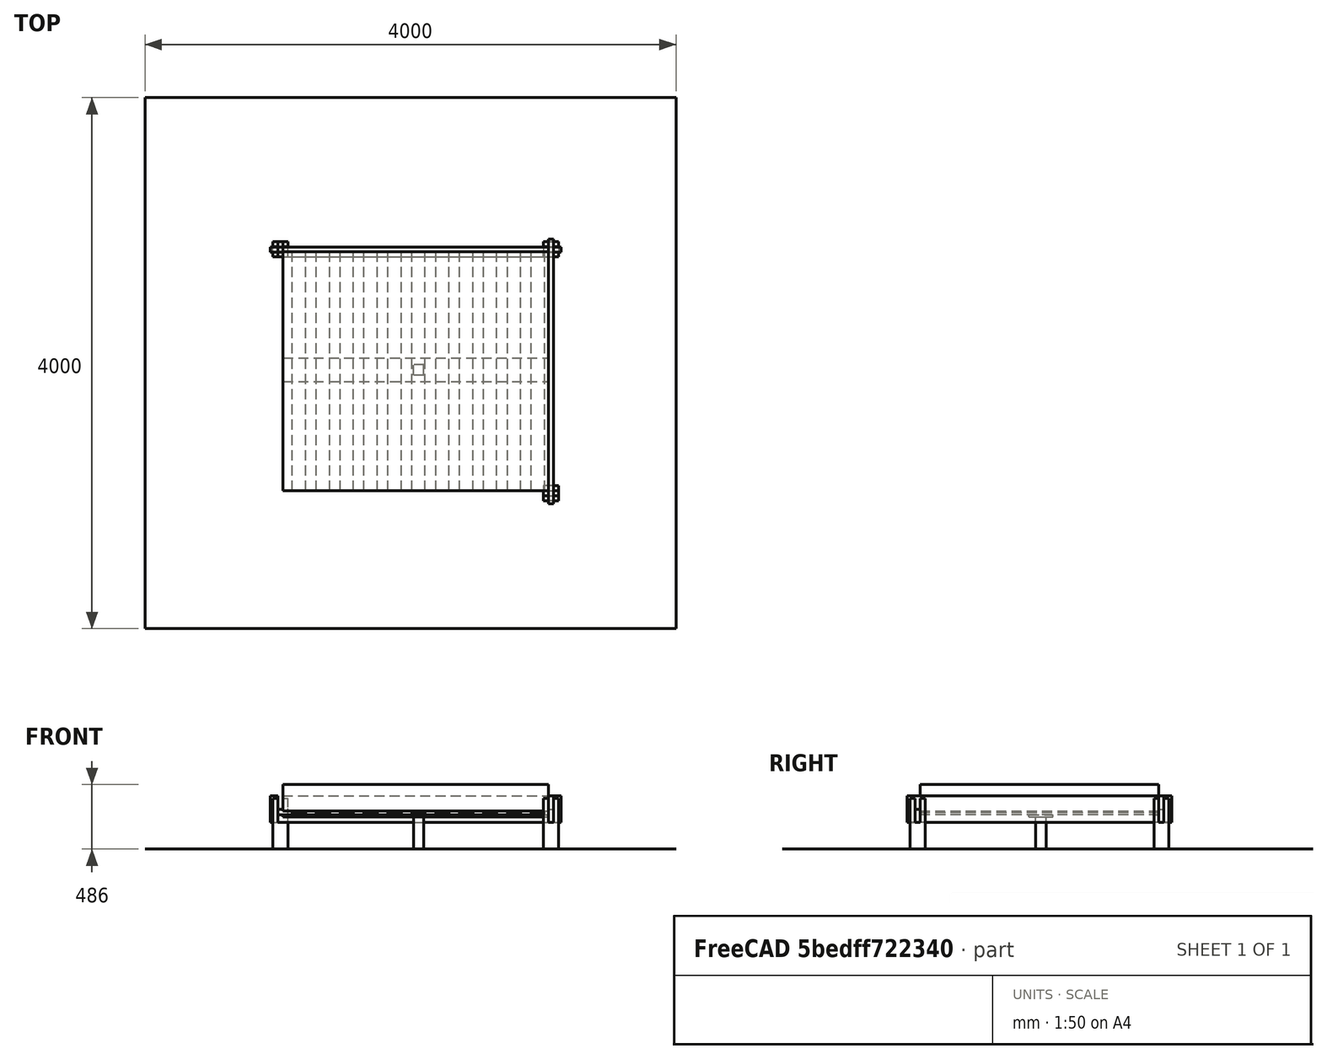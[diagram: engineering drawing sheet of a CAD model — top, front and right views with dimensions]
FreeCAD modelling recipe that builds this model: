
FCSTD DOCUMENT  (FreeCAD 0.18RUnknown)
Label: bett
License: All rights reserved
LicenseURL: http://en.wikipedia.org/wiki/All_rights_reserved
objects: Part::Box×18, TechDraw::DrawViewDimension×15, Part::FeaturePython×7, Part::Cut×4, TechDraw::DrawProjGroup×3, TechDraw::DrawProjGroupItem×2, App::DocumentObjectGroup×2, TechDraw::DrawViewPart×2, Part::MultiFuse×1, TechDraw::DrawSVGTemplate×1, TechDraw::DrawPage×1
note: 30 computed .brp shape members not serialized (recipe doc carries the construction recipe); baked Part::Feature solids carry a one-line shape summary decoded from their .brp

FEATURE [Part::Box] Box  label="Cube"
  AttacherType = Attacher::AttachEngine3D
  Height = 200
  Length = 76
  Width = 76
FEATURE [Part::Box] Box001  label="lang-1"
  AttacherType = Attacher::AttachEngine3D
  Height = 380
  Length = 38
  Placement = pos=(-38,0,0) rot=(0,0,1;0rad)
  Width = 38
FEATURE [Part::Box] Box002  label="lang-2"
  AttacherType = Attacher::AttachEngine3D
  Height = 380
  Length = 38
  Placement = pos=(38,76,0) rot=(0,0,1;0rad)
  Width = 38
FEATURE [Part::Box] Box003  label="lang-3"
  AttacherType = Attacher::AttachEngine3D
  Height = 380
  Length = 38
  Placement = pos=(-38,76,0) rot=(0,0,1;0rad)
  Width = 38
FEATURE [Part::Box] Box004  label="Cube004"
  AttacherType = Attacher::AttachEngine3D
  Height = 200
  Length = 38
  Placement = pos=(-38,38,0) rot=(0,0,1;0rad)
  Width = 38
FEATURE [Part::Box] Box005  label="Cube005"
  AttacherType = Attacher::AttachEngine3D
  Height = 200
  Length = 38
  Placement = pos=(0,76,0) rot=(0,0,1;0rad)
  Width = 38
FEATURE [Part::MultiFuse] Fusion  label="VR"
  Placement = pos=(76,0,0) rot=(0,0,1;1.5708rad)
  Shapes = -> [Box,Box001,Box002,Box003,Box004,Box005]
FEATURE [Part::Box] Box015  label="R"
  AttacherType = Attacher::AttachEngine3D
  Height = 200
  Length = 2192
  Placement = pos=(-58,0,200) rot=(0,0,1;0rad)
  Width = 38
FEATURE [Part::Box] Box017  label="V"
  AttacherType = Attacher::AttachEngine3D
  Height = 200
  Length = 1992
  Placement = pos=(38,-58,200) rot=(0,0,1;1.5708rad)
  Width = 38
FEATURE [Part::Box] Box019  label="Matratze"
  AttacherType = Attacher::AttachEngine3D
  Height = 200
  Length = 2000
  Placement = pos=(38,38,285) rot=(0,0,1;0rad)
  Width = 1800
FEATURE [Part::Box] Box020  label="Querstrebe"
  AttacherType = Attacher::AttachEngine3D
  Height = 18
  Length = 2000
  Placement = pos=(40,860,240) rot=(0,0,1;0rad)
  Width = 180
FEATURE [Part::Box] Box021  label="Mittelpfosten"
  AttacherType = Attacher::AttachEngine3D
  Height = 78
  Length = 240
  Placement = pos=(1100,910,1.63e-13) rot=(0,-1,0;1.5708rad)
  Width = 78
FEATURE [Part::Box] Box022  label="Rost"
  AttacherType = Attacher::AttachEngine3D
  Height = 18
  Length = 1800
  Placement = pos=(110,0,277) rot=(0.707107,0.707107,0;3.14159rad)
  Width = 100
FEATURE [Part::Box] Box023  label="V001"
  AttacherType = Attacher::AttachEngine3D
  Height = 100
  Length = 200
  Placement = pos=(-100,0,200) rot=(0,0,1;0rad)
  Width = 38
FEATURE [Part::Cut] Cut
  Base = -> Box017
  Tool = -> Box023
FEATURE [Part::Box] Box024  label="H001"
  AttacherType = Attacher::AttachEngine3D
  Height = 100
  Length = 200
  Placement = pos=(-100,1838,200) rot=(0,0,1;0rad)
  Width = 38
FEATURE [Part::Cut] Cut001  label="S-V"
  Base = -> Cut
  Tool = -> Box024
FEATURE [Part::Box] Box026  label="L002"
  AttacherType = Attacher::AttachEngine3D
  Height = 100
  Length = 200
  Placement = pos=(38,-100,300) rot=(0,0,1;1.5708rad)
  Width = 38
FEATURE [Part::Cut] Cut003
  Base = -> Box015
  Tool = -> Box026
FEATURE [Part::Box] Box027  label="L003"
  AttacherType = Attacher::AttachEngine3D
  Height = 100
  Length = 200
  Placement = pos=(2076,-100,300) rot=(0,0,1;1.5708rad)
  Width = 38
FEATURE [Part::Cut] Cut004  label="S-R"
  Base = -> Cut003
  Tool = -> Box027
FEATURE [Part::FeaturePython] Array  # Draft array (typed FeaturePython)
  Angle = 360
  ArrayType = 0
  Axis = (0,0,1)
  Base = -> Box022
  Center = (0,0,0)
  Fuse = false
  IntervalAxis = (0,0,0)
  IntervalX = (180,0,0)
  IntervalY = (0,1,0)
  IntervalZ = (0,0,1)
  NumberPolar = 1
  NumberX = 11
  NumberY = 2
  NumberZ = 1
  Placement = pos=(0,38,0) rot=(0,0,1;0rad)
FEATURE [Part::Box] Box031  label="Rostauflage R"
  AttacherType = Attacher::AttachEngine3D
  Height = 58
  Length = 2000
  Placement = pos=(0,38,200) rot=(0,0,1;0rad)
  Width = 38
FEATURE [Part::Box] Box033  label="Boden"
  AttacherType = Attacher::AttachEngine3D
  Height = 1
  Length = 4000
  Placement = pos=(-1000,-1000,-1) rot=(0,0,1;0rad)
  Width = 4000
FEATURE [TechDraw::DrawSVGTemplate] Template
  Height = 210
  Orientation = 1
  Width = 297
FEATURE [TechDraw::DrawProjGroupItem] ProjItem  label="Kurze Seiten"
  CoarseView = false
  Direction = (1,0,0)
  Focus = 100
  HardHidden = false
  IsoCount = 0
  IsoHidden = false
  IsoVisible = false
  LockPosition = true
  Perspective = false
  Rotation = 0
  RotationVector = (0,1,0)
  Scale = 0.1
  ScaleType = 2
  SeamHidden = false
  SeamVisible = false
  SmoothHidden = false
  SmoothVisible = false
  Type = 0
  X = 0
  Y = 0
FEATURE [TechDraw::DrawProjGroup] ProjGroup
  Anchor = -> ProjItem
  AutoDistribute = true
  LockPosition = false
  ProjectionType = 0
  Rotation = 0
  Scale = 0.1
  ScaleType = 0
  Views = -> [ProjItem]
  X = 154.536
  Y = 169.749
  spacingX = 15
  spacingY = 15
FEATURE [TechDraw::DrawViewDimension] Dimension
  Arbitrary = false
  FormatSpec = %.2f
  LockPosition = false
  MeasureType = 1
  OverTolerance = 0
  References2D = -> [ProjItem]
  Rotation = 0
  ScaleType = 0
  Type = 0
  UnderTolerance = 0
  X = 1.3039
  Y = 17.0645
FEATURE [TechDraw::DrawViewDimension] Dimension001
  Arbitrary = false
  FormatSpec = %.2f
  LockPosition = false
  MeasureType = 1
  OverTolerance = 0
  References2D = -> [ProjItem]
  Rotation = 0
  ScaleType = 0
  Type = 2
  UnderTolerance = 0
  X = -85.072
  Y = 0.024594
FEATURE [TechDraw::DrawViewDimension] Dimension002
  Arbitrary = false
  FormatSpec = %.2f
  LockPosition = false
  MeasureType = 1
  OverTolerance = 0
  References2D = -> [ProjItem]
  Rotation = 0
  ScaleType = 0
  Type = 1
  UnderTolerance = 0
  X = -110.228
  Y = -12.9954
FEATURE [TechDraw::DrawViewDimension] Dimension003
  Arbitrary = false
  FormatSpec = %.2f
  LockPosition = false
  MeasureType = 1
  OverTolerance = 0
  References2D = -> [ProjItem]
  Rotation = 0
  ScaleType = 0
  Type = 1
  UnderTolerance = 0
  X = -79.3385
  Y = -19.6627
FEATURE [TechDraw::DrawViewDimension] Dimension004
  Arbitrary = false
  FormatSpec = %.2f
  LockPosition = false
  MeasureType = 1
  OverTolerance = 0
  References2D = -> [ProjItem]
  Rotation = 0
  ScaleType = 0
  Type = 2
  UnderTolerance = 0
  X = -107.983
  Y = 0.457269
FEATURE [TechDraw::DrawProjGroupItem] ProjItem001  label="Lange Seiten"
  CoarseView = false
  Direction = (0,-1,0)
  Focus = 100
  HardHidden = false
  IsoCount = 0
  IsoHidden = false
  IsoVisible = false
  LockPosition = true
  Perspective = false
  Rotation = 0
  RotationVector = (1,0,0)
  Scale = 0.1
  ScaleType = 2
  SeamHidden = false
  SeamVisible = false
  SmoothHidden = false
  SmoothVisible = false
  Source = -> [Cut004]
  Type = 0
  X = 0
  Y = 0
FEATURE [TechDraw::DrawProjGroup] ProjGroup001
  Anchor = -> ProjItem001
  AutoDistribute = true
  LockPosition = false
  ProjectionType = 0
  Rotation = 0
  Scale = 0.1
  ScaleType = 0
  Source = -> [Cut004]
  Views = -> [ProjItem001]
  X = 156.289
  Y = 114.626
  spacingX = 15
  spacingY = 15
FEATURE [TechDraw::DrawViewDimension] Dimension005
  Arbitrary = false
  FormatSpec = %.2f
  LockPosition = false
  MeasureType = 1
  OverTolerance = 0
  References2D = -> [ProjItem001]
  Rotation = 0
  ScaleType = 0
  Type = 1
  UnderTolerance = 0
  X = -120.062
  Y = 24.2428
FEATURE [TechDraw::DrawViewDimension] Dimension006
  Arbitrary = false
  FormatSpec = %.2f
  LockPosition = false
  MeasureType = 1
  OverTolerance = 0
  References2D = -> [ProjItem001]
  Rotation = 0
  ScaleType = 0
  Type = 1
  UnderTolerance = 0
  X = -88.9728
  Y = 19.6663
FEATURE [TechDraw::DrawViewDimension] Dimension007
  Arbitrary = false
  FormatSpec = %.2f
  LockPosition = false
  MeasureType = 1
  OverTolerance = 0
  References2D = -> [ProjItem001]
  Rotation = 0
  ScaleType = 0
  Type = 2
  UnderTolerance = 0
  X = -95.9239
  Y = -0.007839
FEATURE [TechDraw::DrawViewDimension] Dimension008
  Arbitrary = false
  FormatSpec = %.2f
  LockPosition = false
  MeasureType = 1
  OverTolerance = 0
  References2D = -> [ProjItem001]
  Rotation = 0
  ScaleType = 0
  Type = 1
  UnderTolerance = 0
  X = -1.80037
  Y = -13.564
FEATURE [TechDraw::DrawProjGroup] ProjGroup002
  AutoDistribute = true
  LockPosition = false
  ProjectionType = 0
  Rotation = 0
  Scale = 0.1
  ScaleType = 0
  X = 51.6303
  Y = 56.7766
  spacingX = 15
  spacingY = 15
FEATURE [TechDraw::DrawViewDimension] Dimension009
  Arbitrary = false
  FormatSpec = %.2f
  LockPosition = false
  MeasureType = 1
  OverTolerance = 0
  References2D = -> [ProjItem001]
  Rotation = 0
  ScaleType = 0
  Type = 2
  UnderTolerance = 0
  X = -117.994
  Y = -0.079621
FEATURE [Part::FeaturePython] Clone  label="VL"  # Draft clone (typed FeaturePython)
  AttacherType = Attacher::AttachEngine3D
  Fuse = false
  Objects = -> [Fusion]
  Placement = pos=(0,1800,0) rot=(0,0,1;0rad)
  Scale = (1,1,1)
FEATURE [Part::FeaturePython] Clone001  label="HL"  # Draft clone (typed FeaturePython)
  AttacherType = Attacher::AttachEngine3D
  Fuse = false
  Objects = -> [Fusion]
  Placement = pos=(2000,1876,0) rot=(0,0,1;4.71239rad)
  Scale = (1,1,1)
FEATURE [Part::FeaturePython] Clone002  label="HR"  # Draft clone (typed FeaturePython)
  AttacherType = Attacher::AttachEngine3D
  Fuse = false
  Objects = -> [Fusion]
  Placement = pos=(2076,76,0) rot=(0,0,1;3.14159rad)
  Scale = (1,1,1)
FEATURE [App::DocumentObjectGroup] Group002  label="Pfosten"
  Group = -> [Fusion,Clone,Clone001,Clone002]
FEATURE [Part::FeaturePython] Clone003  label="S-H"  # Draft clone (typed FeaturePython)
  AttacherType = Attacher::AttachEngine3D
  Fuse = false
  Objects = -> [Cut001]
  Placement = pos=(2038,0,0) rot=(0,0,1;0rad)
  Scale = (1,1,1)
FEATURE [Part::FeaturePython] Clone004  label="S-L"  # Draft clone (typed FeaturePython)
  AttacherType = Attacher::AttachEngine3D
  Fuse = false
  Objects = -> [Cut004]
  Placement = pos=(0,1836,0) rot=(0,0,1;0rad)
  Scale = (1,1,1)
FEATURE [Part::FeaturePython] Clone005  label="Rostauflage L"  # Draft clone (typed FeaturePython)
  AttacherType = Attacher::AttachEngine3D
  Fuse = false
  Objects = -> [Box031]
  Placement = pos=(0,1800,200) rot=(0,0,1;0rad)
  Scale = (1,1,1)
FEATURE [App::DocumentObjectGroup] Group003  label="Seiten"
  Group = -> [Cut001,Cut004,Clone003,Clone004,Box031,Clone005]
FEATURE [TechDraw::DrawViewPart] View001
  CoarseView = false
  Direction = (0,-1,0)
  Focus = 100
  HardHidden = false
  IsoCount = 0
  IsoHidden = false
  IsoVisible = false
  LockPosition = false
  Perspective = false
  Rotation = 0
  Scale = 0.1
  ScaleType = 0
  SeamHidden = false
  SeamVisible = false
  SmoothHidden = false
  SmoothVisible = false
  Source = -> [Fusion]
  X = 126.324
  Y = 42.2621
FEATURE [TechDraw::DrawViewDimension] Dimension010
  Arbitrary = false
  FormatSpec = %.2f
  LockPosition = false
  MeasureType = 1
  OverTolerance = 0
  References2D = -> [View001]
  Rotation = 0
  ScaleType = 0
  Type = 2
  UnderTolerance = 0
  X = 9.33409
  Y = -0.641311
FEATURE [TechDraw::DrawViewDimension] Dimension011
  Arbitrary = false
  FormatSpec = %.2f
  LockPosition = false
  MeasureType = 1
  OverTolerance = 0
  References2D = -> [View001]
  Rotation = 0
  ScaleType = 0
  Type = 1
  UnderTolerance = 0
  X = -3.47934
  Y = 39.7357
FEATURE [TechDraw::DrawViewDimension] Dimension012
  Arbitrary = false
  FormatSpec = %.2f
  LockPosition = false
  MeasureType = 1
  OverTolerance = 0
  References2D = -> [View001]
  Rotation = 0
  ScaleType = 0
  Type = 1
  UnderTolerance = 0
  X = 11.7574
  Y = 33.6433
FEATURE [TechDraw::DrawViewDimension] Dimension013
  Arbitrary = false
  FormatSpec = %.2f
  LockPosition = false
  MeasureType = 1
  OverTolerance = 0
  References2D = -> [View001]
  Rotation = 0
  ScaleType = 0
  Type = 1
  UnderTolerance = 0
  X = 15.2367
  Y = 26.8026
FEATURE [TechDraw::DrawViewDimension] Dimension014
  Arbitrary = false
  FormatSpec = %.2f
  LockPosition = false
  MeasureType = 1
  OverTolerance = 0
  References2D = -> [View001]
  Rotation = 0
  ScaleType = 0
  Type = 2
  UnderTolerance = 0
  X = -13.8711
  Y = -8.03803
FEATURE [TechDraw::DrawViewPart] View
  CoarseView = false
  Direction = (0.331,0.893,0.305)
  Focus = 100
  HardHidden = false
  IsoCount = 0
  IsoHidden = false
  IsoVisible = false
  LockPosition = false
  Perspective = false
  Rotation = 0
  Scale = 0.1
  ScaleType = 2
  SeamHidden = false
  SeamVisible = false
  SmoothHidden = false
  SmoothVisible = false
  Source = -> [Fusion]
  X = 93.7575
  Y = 44.96
FEATURE [TechDraw::DrawPage] Page
  KeepUpdated = true
  ProjectionType = 0
  Template = -> Template
  Views = -> [ProjGroup,Dimension,Dimension001,Dimension002,Dimension003,Dimension004,ProjGroup001,Dimension005,Dimension006,Dimension007,Dimension008,ProjGroup002,Dimension009,View,View001,Dimension010,Dimension011,Dimension012,Dimension013,Dimension014]
